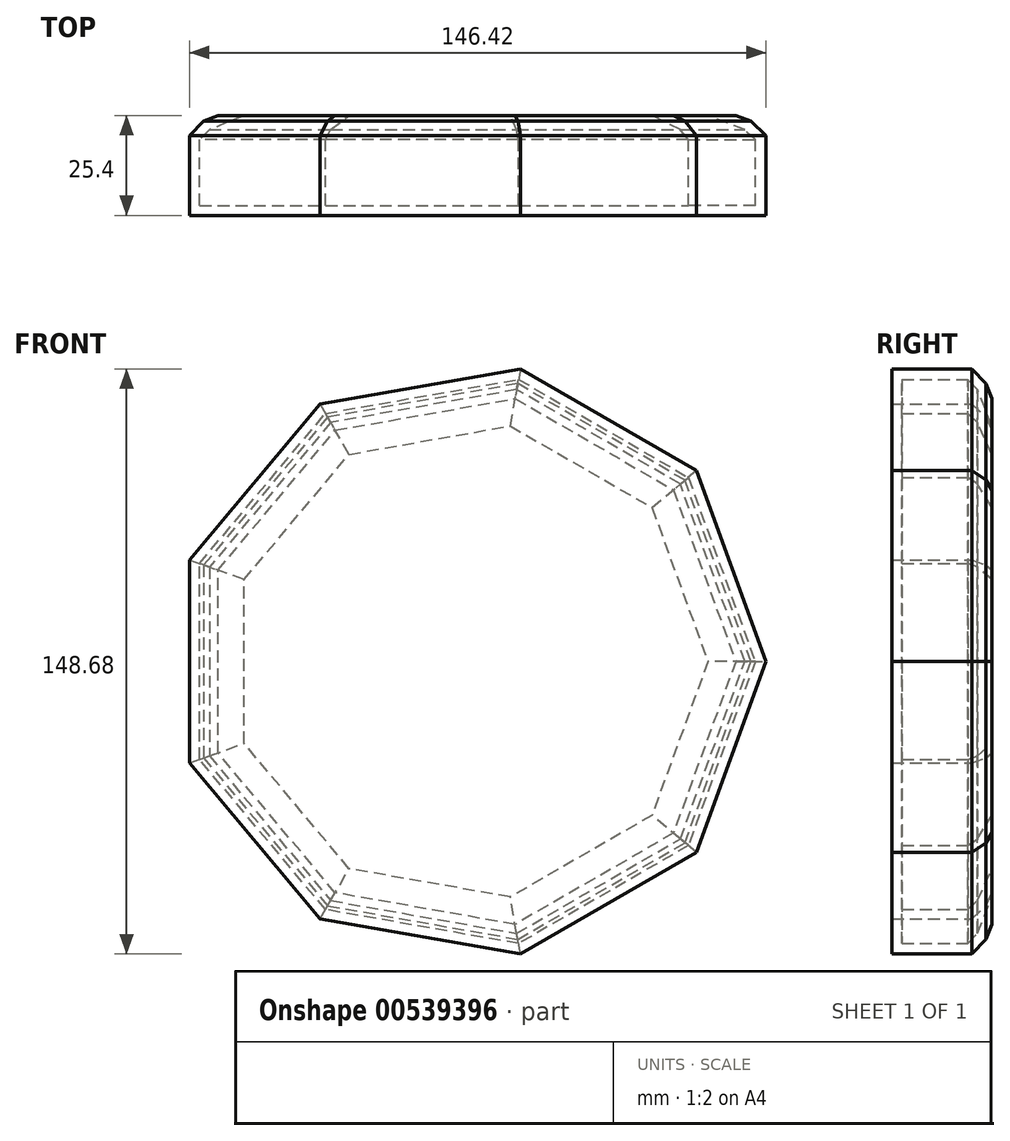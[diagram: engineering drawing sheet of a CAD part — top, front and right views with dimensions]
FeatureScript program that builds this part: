
annotation { "Feature Type Name" : "Feature", "Feature Type Description" : "" }
export const myFeature = defineFeature(function(context is Context, id is Id, definition is map)
    precondition{}
    {
        {
            var Q0;
            Q0=qCreatedBy(makeId("Front.planeOp"),FACE);
            var sketch = newSketch(context, id + "F0", { "sketchPlane" : qUnion([Q0])});
            skCircle(sketch, "E0.cCircle", {"center": v(0, 0) * mm, "radius": 75.49 * mm, "construction": true});
            skLineSegment(sketch, "E0.0", {"start": v(75.49, 0) * mm, "end": v(57.83, -48.52) * mm});
            skLineSegment(sketch, "E0.1", {"start": v(57.83, -48.52) * mm, "end": v(13.1, -74.34) * mm});
            skLineSegment(sketch, "E0.2", {"start": v(13.1, -74.34) * mm, "end": v(-37.74, -65.37) * mm});
            skLineSegment(sketch, "E0.3", {"start": v(-37.74, -65.37) * mm, "end": v(-70.93, -25.82) * mm});
            skLineSegment(sketch, "E0.4", {"start": v(-70.93, -25.82) * mm, "end": v(-70.93, 25.82) * mm});
            skLineSegment(sketch, "E0.5", {"start": v(-70.93, 25.82) * mm, "end": v(-37.74, 65.37) * mm});
            skLineSegment(sketch, "E0.6", {"start": v(-37.74, 65.37) * mm, "end": v(13.1, 74.34) * mm});
            skLineSegment(sketch, "E0.7", {"start": v(13.1, 74.34) * mm, "end": v(57.83, 48.52) * mm});
            skLineSegment(sketch, "E0.8", {"start": v(57.83, 48.52) * mm, "end": v(75.49, 0) * mm});
            skSolve(sketch);
        }
        {
            var Q0;
            Q0 = qSketchRegion(id + "F0", true);
            extrude(context, id + "F1", {"entities" : qUnion([Q0]), "depth" : 25.4 * mm, "offsetDistance" : 25.4 * mm});
        }
        {
            var Q0;
            Q0=makeQuery(id+"F1.opExtrude","CAP_FACE",FACE,{"disambiguationData":[OSD([sQuery(id+"F0.wireOp",EDGE,"E0.0"),sQuery(id+"F0.wireOp",EDGE,"E0.1"),sQuery(id+"F0.wireOp",EDGE,"E0.2"),sQuery(id+"F0.wireOp",EDGE,"E0.3"),sQuery(id+"F0.wireOp",EDGE,"E0.4"),sQuery(id+"F0.wireOp",EDGE,"E0.5"),sQuery(id+"F0.wireOp",EDGE,"E0.6"),sQuery(id+"F0.wireOp",EDGE,"E0.7"),sQuery(id+"F0.wireOp",EDGE,"E0.8")])],"isStart":true});
            chamfer(context, id + "F2", {"entities" : qUnion([Q0]), "chamferType" : ChamferType.TWO_OFFSETS, "width1" : 5.08 * mm, "oppositeDirection" : true, "width2" : 5.08 * mm, "tangentPropagation" : true});
        }
        {
            var Q0;
            Q0=makeQuery(id+"F1.opExtrude","CAP_FACE",FACE,{"disambiguationData":[OSD([sQuery(id+"F0.wireOp",EDGE,"E0.0"),sQuery(id+"F0.wireOp",EDGE,"E0.1"),sQuery(id+"F0.wireOp",EDGE,"E0.2"),sQuery(id+"F0.wireOp",EDGE,"E0.3"),sQuery(id+"F0.wireOp",EDGE,"E0.4"),sQuery(id+"F0.wireOp",EDGE,"E0.5"),sQuery(id+"F0.wireOp",EDGE,"E0.6"),sQuery(id+"F0.wireOp",EDGE,"E0.7"),sQuery(id+"F0.wireOp",EDGE,"E0.8")])],"isStart":true});
            chamfer(context, id + "F3", {"entities" : qUnion([Q0]), "width" : 5.08 * mm, "tangentPropagation" : true});
        }
        {
            var Q0;
            Q0=makeQuery(id+"F1.opExtrude","CAP_FACE",FACE,{"disambiguationData":[OSD([sQuery(id+"F0.wireOp",EDGE,"E0.0"),sQuery(id+"F0.wireOp",EDGE,"E0.1"),sQuery(id+"F0.wireOp",EDGE,"E0.2"),sQuery(id+"F0.wireOp",EDGE,"E0.3"),sQuery(id+"F0.wireOp",EDGE,"E0.4"),sQuery(id+"F0.wireOp",EDGE,"E0.5"),sQuery(id+"F0.wireOp",EDGE,"E0.6"),sQuery(id+"F0.wireOp",EDGE,"E0.7"),sQuery(id+"F0.wireOp",EDGE,"E0.8")])],"isStart":true});
            shell(context, id + "F4", {"entities" : qUnion([Q0]), "thickness" : 2.54 * mm});
        }
    });
